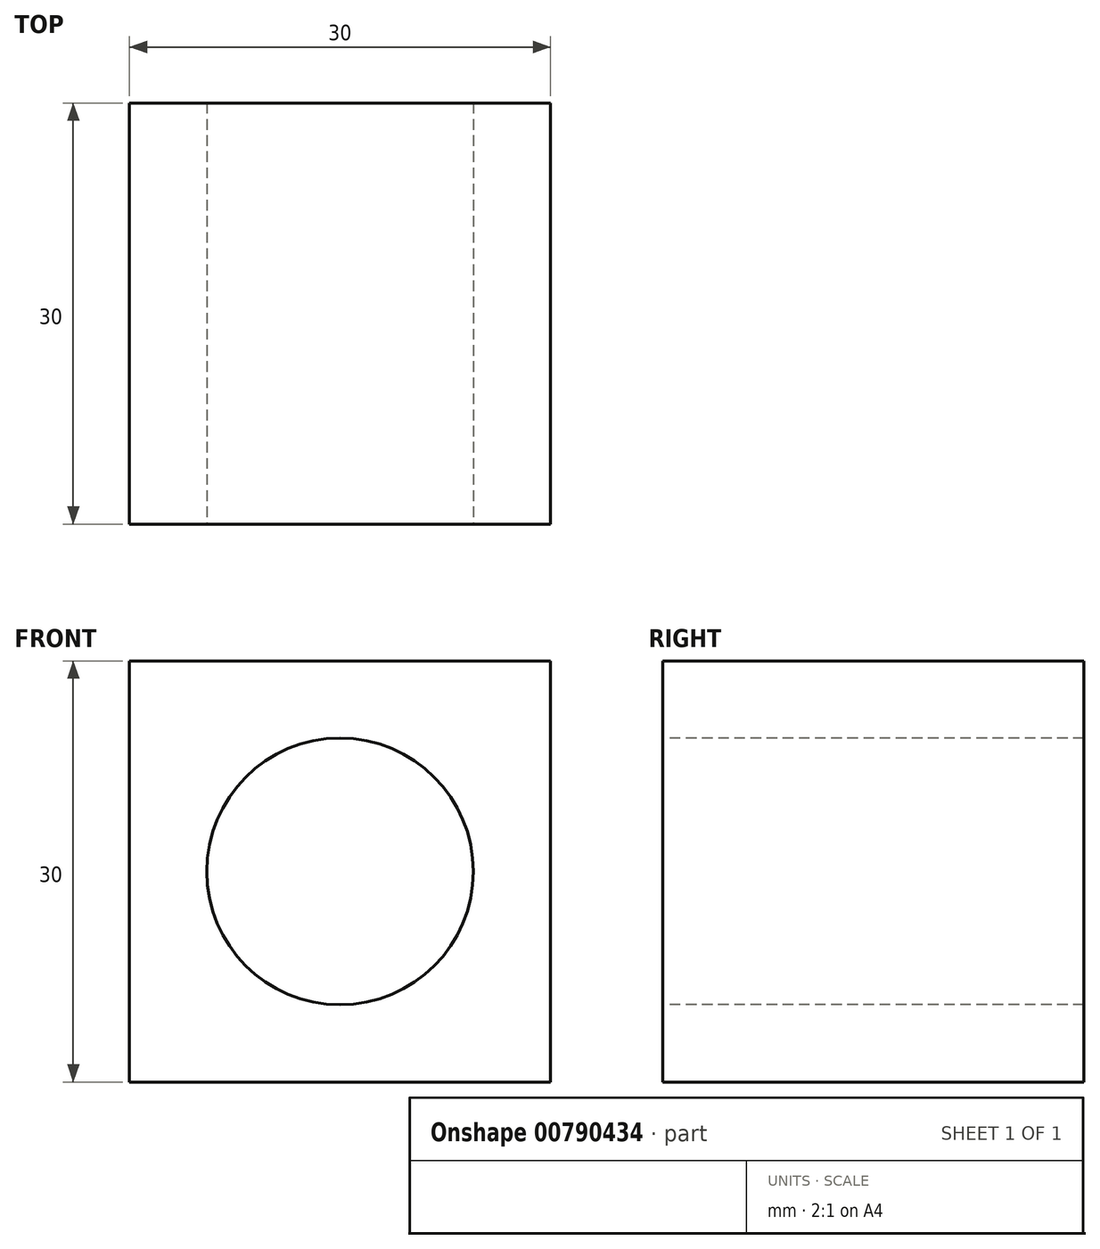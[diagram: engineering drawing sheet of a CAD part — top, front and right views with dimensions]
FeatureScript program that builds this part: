
annotation { "Feature Type Name" : "Feature", "Feature Type Description" : "" }
export const myFeature = defineFeature(function(context is Context, id is Id, definition is map)
    precondition{}
    {
        {
            var Q0;
            Q0=qCreatedBy(makeId("Front.planeOp"),FACE);
            var sketch = newSketch(context, id + "F0", { "sketchPlane" : qUnion([Q0])});
            skLineSegment(sketch, "E0.bottom", {"start": v(0, 0) * mm, "end": v(30, 0) * mm});
            skLineSegment(sketch, "E0.top", {"start": v(0, 30) * mm, "end": v(30, 30) * mm});
            skLineSegment(sketch, "E0.left", {"start": v(0, 0) * mm, "end": v(0, 30) * mm});
            skLineSegment(sketch, "E0.right", {"start": v(30, 0) * mm, "end": v(30, 30) * mm});
            skSolve(sketch);
        }
        {
            var Q0;
            Q0 = qSketchRegion(id + "F0", true);
            extrude(context, id + "F1", {"entities" : qUnion([Q0]), "depth" : 30 * mm, "offsetDistance" : 25 * mm});
        }
        {
            var Q0;
            Q0=makeQuery(id+"F1.opExtrude","CAP_FACE",FACE,{"disambiguationData":[OSD([sQuery(id+"F0.wireOp",EDGE,"E0.bottom"),sQuery(id+"F0.wireOp",EDGE,"E0.top"),sQuery(id+"F0.wireOp",EDGE,"E0.left"),sQuery(id+"F0.wireOp",EDGE,"E0.right")])],"isStart":false});
            var sketch = newSketch(context, id + "F2", { "sketchPlane" : qUnion([Q0])});
            skCircle(sketch, "E1", {"center": v(15, 15) * mm, "radius": 9.5 * mm});
            skPoint(sketch, "E1.centerSnap0", {"position": v(30, 15) * mm});
            skPoint(sketch, "E1.centerSnap1", {"position": v(15, 30) * mm});
            skSolve(sketch);
        }
        {
            var Q0;
            Q0=makeQuery(id+"F2.imprint","IMPRINT",FACE,{"disambiguationData":[TD([[makeQuery(id+"F2.imprint","IMPRINT",EDGE,{"derivedFrom":sQuery(id+"F2.wireOp",EDGE,"E1")}),1.0]])]});
            extrude(context, id + "F3", {"entities" : qUnion([Q0]), "operationType" : NewBodyOperationType.REMOVE, "oppositeDirection" : true, "depth" : 30 * mm, "offsetDistance" : 25 * mm});
        }
    });
